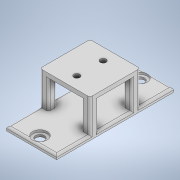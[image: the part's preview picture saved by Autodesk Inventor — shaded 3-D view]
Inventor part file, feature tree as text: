
AUTODESK INVENTOR PART (.ipt)
format: ipt  version: 2020 (Build 240168000, 168)  size: 207,872 bytes
history: native  units: in
note: dims shown in document units (in); Inventor stores cm internally (conversion verified against a paired STEP export)
features: sketch x5, extrude x3, hole x2, fillet x1
ambient origin geometry x8: Origin, YZ Plane, XZ Plane, XY Plane, X Axis, Y Axis, Z Axis, Center Point
bodies: Solid1 (feature_tree)
feature tree (11):
  extrude  "Extrusion1"  Depth=1.5in
  hole  "Hole1"  [1 undecoded]
  extrude  "Extrusion2"  Depth=0.3937in
  extrude  "Extrusion3"  Depth=0.25in
  hole  "Hole2"  [1 undecoded]
  fillet  "Fillet1"  Radius=0.25in
  sketch  "Sketch2"  dims[d0=1.5in d1=1.5in]
  sketch  "Sketch3"  dims[d2=0.125in d3=0.0in d4=0.75in]
  sketch  "Sketch4"  dims[d5=0.3937in d6=0.7874in]
  sketch  "Sketch5"  dims[d7=0.177in d8=0.75in d9=0.279in d10=0.25in d11=0.5635in d12=0.3898in d13=0.0in d14=0.25in]
  sketch  "Sketch6"  dims[d15=0.25in d16=0.25in d17=0.25in d18=0.25in d19=0.25in d20=0.25in d21=0.25in d22=1.0in d23=0.0in d24=1.5in d25=2.5in d26=1.0in d27=0.125in d28=0.0in d29=1.75in d30=0.75in d31=1.5in d32=3.0in d33=0.266in d34=0.75in d35=0.438in d36=0.0625in d37=0.5635in d38=0.3898in d39=0.0in d40=0.0625in]
note: 2 required parameter values undecoded (feature->parameter linkage not recoverable at this tier; creation-order binding heuristic only, values carry confidence <= 0.55)
